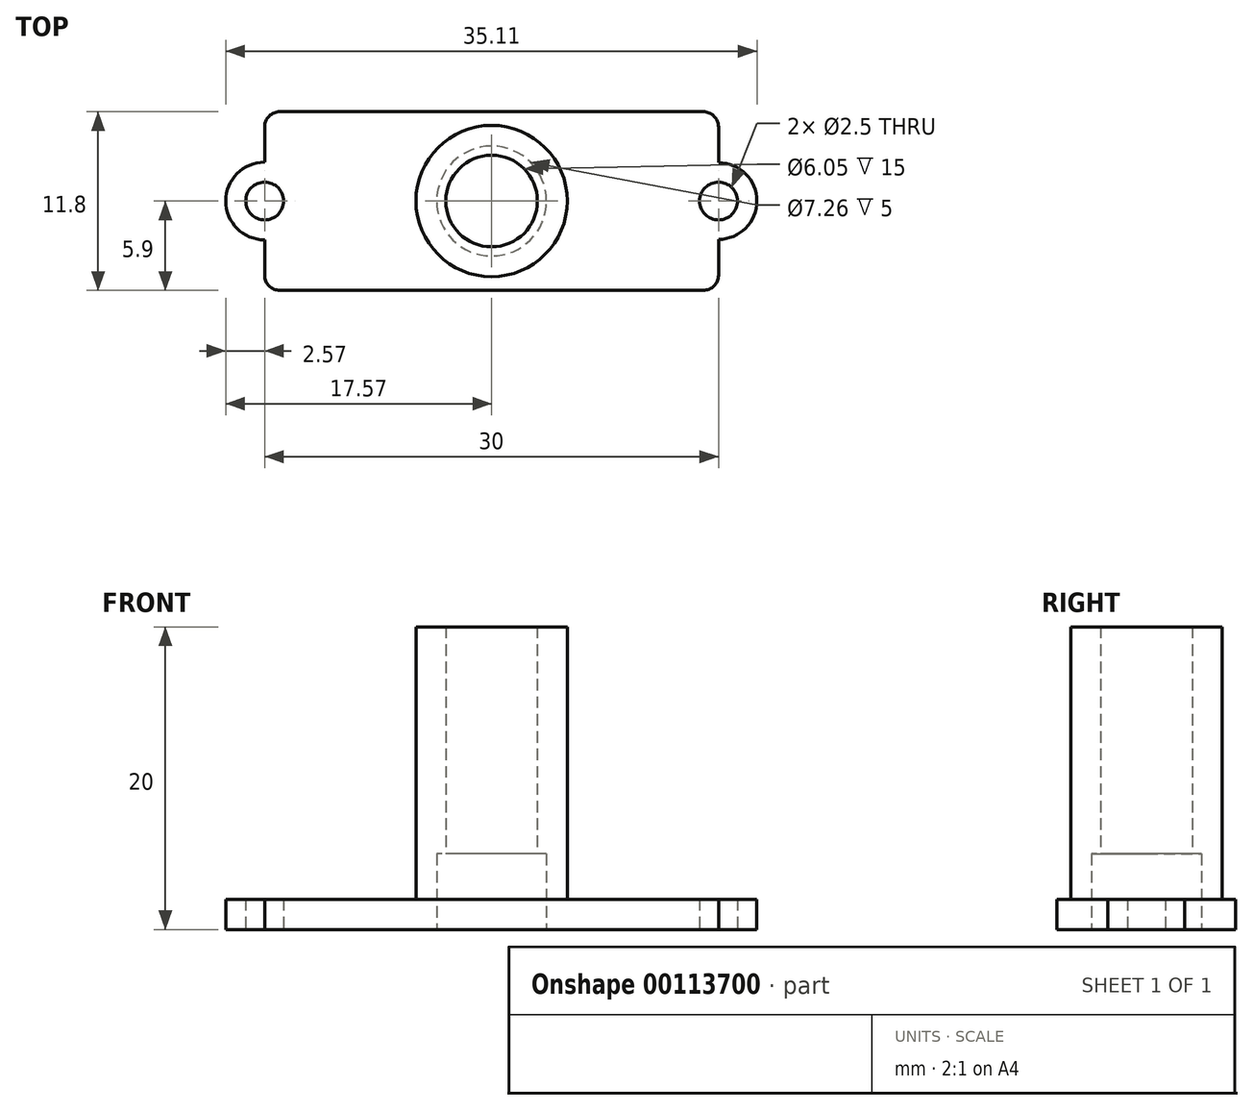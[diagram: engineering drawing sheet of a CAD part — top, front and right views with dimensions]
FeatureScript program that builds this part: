
annotation { "Feature Type Name" : "Feature", "Feature Type Description" : "" }
export const myFeature = defineFeature(function(context is Context, id is Id, definition is map)
    precondition{}
    {
        {
            var Q0;
            Q0=qCreatedBy(makeId("Top.planeOp"),FACE);
            var sketch = newSketch(context, id + "F0", { "sketchPlane" : qUnion([Q0])});
            skLineSegment(sketch, "E0.bottom", {"start": v(14, -5.9) * mm, "end": v(-14, -5.9) * mm});
            skLineSegment(sketch, "E0.top", {"start": v(14, 5.9) * mm, "end": v(-14, 5.9) * mm});
            skLineSegment(sketch, "E0.left", {"start": v(15, -4.9) * mm, "end": v(15, -2.54) * mm});
            skLineSegment(sketch, "E0.right", {"start": v(-15, -4.9) * mm, "end": v(-15, -2.57) * mm});
            skPoint(sketch, "E0.middle", {"position": v(0, 0) * mm});
            skArc(sketch, "E1", {"start": v(-15, 2.57) * mm, "mid": v(-17.57, 0) * mm, "end": v(-15, -2.57) * mm});
            skArc(sketch, "E2", {"start": v(15, -2.54) * mm, "mid": v(17.54, 0) * mm, "end": v(15, 2.54) * mm});
            skCircle(sketch, "E3", {"center": v(0, 0) * mm, "radius": 3.03 * mm});
            skPoint(sketch, "E4.visualSharp", {"position": v(-15, 5.9) * mm});
            skArc(sketch, "E4.filletArc", {"start": v(-14, 5.9) * mm, "mid": v(-14.7, 5.6) * mm, "end": v(-15, 4.9) * mm});
            skPoint(sketch, "E5.visualSharp", {"position": v(-15, -5.9) * mm});
            skArc(sketch, "E5.filletArc", {"start": v(-15, -4.9) * mm, "mid": v(-14.7, -5.6) * mm, "end": v(-14, -5.9) * mm});
            skPoint(sketch, "E6.visualSharp", {"position": v(15, -5.9) * mm});
            skArc(sketch, "E6.filletArc", {"start": v(14, -5.9) * mm, "mid": v(14.7, -5.6) * mm, "end": v(15, -4.9) * mm});
            skPoint(sketch, "E7.visualSharp", {"position": v(15, 5.9) * mm});
            skArc(sketch, "E7.filletArc", {"start": v(15, 4.9) * mm, "mid": v(14.7, 5.6) * mm, "end": v(14, 5.9) * mm});
            skLineSegment(sketch, "E8.trimOffspring", {"start": v(15, 2.54) * mm, "end": v(15, 4.9) * mm});
            skLineSegment(sketch, "E9.trimOffspring", {"start": v(-15, 2.57) * mm, "end": v(-15, 4.9) * mm});
            skCircle(sketch, "E10", {"center": v(0, 0) * mm, "radius": 5 * mm});
            skCircle(sketch, "E11", {"center": v(0, 0) * mm, "radius": 3.63 * mm});
            skSolve(sketch);
        }
        {
            var Q0;
            Q0=makeQuery(id+"F0.imprint","IMPRINT",FACE,{"disambiguationData":[TD([[makeQuery(id+"F0.imprint","IMPRINT",EDGE,{"derivedFrom":sQuery(id+"F0.wireOp",EDGE,"E0.bottom")}),-1.0]])]});
            var Q1;
            Q1=makeQuery(id+"F0.imprint","IMPRINT",FACE,{"disambiguationData":[TD([[makeQuery(id+"F0.imprint","IMPRINT",EDGE,{"derivedFrom":sQuery(id+"F0.wireOp",EDGE,"E10")}),1.0]])]});
            var Q2;
            Q2=makeQuery(id+"F0.imprint","IMPRINT",FACE,{"disambiguationData":[TD([[makeQuery(id+"F0.imprint","IMPRINT",EDGE,{"derivedFrom":sQuery(id+"F0.wireOp",EDGE,"E3")}),-1.0]])]});
            extrude(context, id + "F1", {"entities" : qUnion([Q0, Q1, Q2]), "depth" : 2 * mm});
        }
        {
            var Q0;
            Q0=makeQuery(id+"F0.imprint","IMPRINT",FACE,{"disambiguationData":[TD([[makeQuery(id+"F0.imprint","IMPRINT",EDGE,{"derivedFrom":sQuery(id+"F0.wireOp",EDGE,"E3")}),-1.0]])]});
            var Q1;
            Q1=makeQuery(id+"F0.imprint","IMPRINT",FACE,{"disambiguationData":[TD([[makeQuery(id+"F0.imprint","IMPRINT",EDGE,{"derivedFrom":sQuery(id+"F0.wireOp",EDGE,"E10")}),1.0]])]});
            extrude(context, id + "F2", {"entities" : qUnion([Q0, Q1]), "operationType" : NewBodyOperationType.ADD, "depth" : 20 * mm});
        }
        {
            var Q0;
            Q0=sQuery(id+"F0.wireOp",VERTEX,"E1.center");
            var Q1;
            Q1=sQuery(id+"F0.wireOp",VERTEX,"E2.center");
            var Q2;
            Q2=makeQuery(id+"F1.opExtrude","SWEPT_BODY",BODY,{"disambiguationData":[OSD([sQuery(id+"F0.wireOp",EDGE,"E0.bottom"),sQuery(id+"F0.wireOp",EDGE,"E0.top"),sQuery(id+"F0.wireOp",EDGE,"E0.left"),sQuery(id+"F0.wireOp",EDGE,"E0.right"),sQuery(id+"F0.wireOp",EDGE,"E1"),sQuery(id+"F0.wireOp",EDGE,"E2"),sQuery(id+"F0.wireOp",EDGE,"E3"),sQuery(id+"F0.wireOp",EDGE,"E4.filletArc"),sQuery(id+"F0.wireOp",EDGE,"E5.filletArc"),sQuery(id+"F0.wireOp",EDGE,"E6.filletArc"),sQuery(id+"F0.wireOp",EDGE,"E7.filletArc"),sQuery(id+"F0.wireOp",EDGE,"E8.trimOffspring"),sQuery(id+"F0.wireOp",EDGE,"E9.trimOffspring")])]});
            hole(context, id + "F3", {"style" : HoleStyle.SIMPLE, "endStyle" : HoleEndStyle.BLIND, "oppositeDirection" : true, "holeDiameter" : 2.5 * mm, "holeDepth" : 10 * mm, "locations" : qUnion([Q0, Q1]), "scope" : qUnion([Q2])});
        }
        {
            var Q0;
            Q0=makeQuery(id+"F0.imprint","IMPRINT",FACE,{"disambiguationData":[TD([[makeQuery(id+"F0.imprint","IMPRINT",EDGE,{"derivedFrom":sQuery(id+"F0.wireOp",EDGE,"E3")}),-1.0]])]});
            extrude(context, id + "F4", {"entities" : qUnion([Q0]), "operationType" : NewBodyOperationType.REMOVE, "depth" : 5 * mm});
        }
    });
